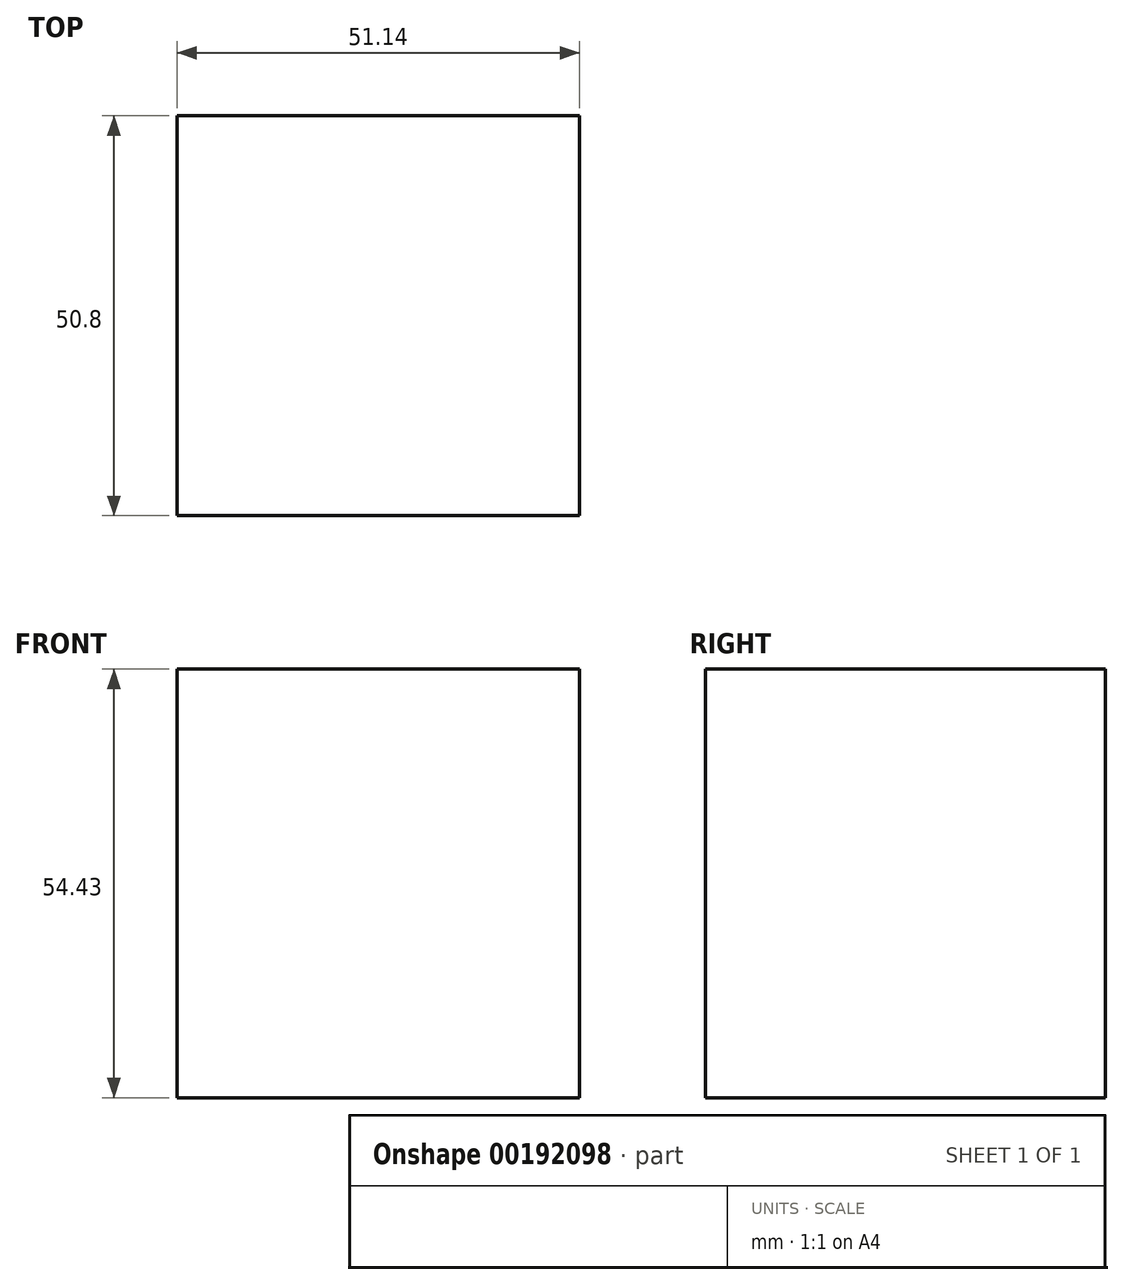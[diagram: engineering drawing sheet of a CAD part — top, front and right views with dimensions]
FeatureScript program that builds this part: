
annotation { "Feature Type Name" : "Feature", "Feature Type Description" : "" }
export const myFeature = defineFeature(function(context is Context, id is Id, definition is map)
    precondition{}
    {
        {
            var Q0;
            Q0=qCreatedBy(makeId("Front.planeOp"),FACE);
            var sketch = newSketch(context, id + "F0", { "sketchPlane" : qUnion([Q0])});
            skLineSegment(sketch, "E0.bottom", {"start": v(-18.48, 20.45) * mm, "end": v(32.66, 20.45) * mm});
            skLineSegment(sketch, "E0.top", {"start": v(-18.48, -33.98) * mm, "end": v(32.66, -33.98) * mm});
            skLineSegment(sketch, "E0.left", {"start": v(-18.48, 20.45) * mm, "end": v(-18.48, -33.98) * mm});
            skLineSegment(sketch, "E0.right", {"start": v(32.66, 20.45) * mm, "end": v(32.66, -33.98) * mm});
            skCircle(sketch, "E1", {"center": v(5.16, -4.53) * mm, "radius": 12.9 * mm});
            skSolve(sketch);
        }
        {
            var Q0;
            Q0=makeQuery(id+"F0.imprint","IMPRINT",FACE,{"disambiguationData":[TD([[makeQuery(id+"F0.imprint","IMPRINT",EDGE,{"derivedFrom":sQuery(id+"F0.wireOp",EDGE,"E0.bottom")}),-1.0]])]});
            var Q1;
            Q1=makeQuery(id+"F0.imprint","IMPRINT",FACE,{"disambiguationData":[TD([[makeQuery(id+"F0.imprint","IMPRINT",EDGE,{"derivedFrom":sQuery(id+"F0.wireOp",EDGE,"E1")}),1.0]])]});
            extrude(context, id + "F1", {"entities" : qUnion([Q0, Q1]), "depth" : 25.4 * mm});
        }
        {
            var Q0;
            Q0=makeQuery(id+"F1.opExtrude","CAP_FACE",FACE,{"disambiguationData":[OSD([sQuery(id+"F0.wireOp",EDGE,"E0.bottom"),sQuery(id+"F0.wireOp",EDGE,"E0.top"),sQuery(id+"F0.wireOp",EDGE,"E0.left"),sQuery(id+"F0.wireOp",EDGE,"E0.right")])],"isStart":true});
            extrude(context, id + "F2", {"entities" : qUnion([Q0]), "operationType" : NewBodyOperationType.ADD, "depth" : 25.4 * mm});
        }
    });
